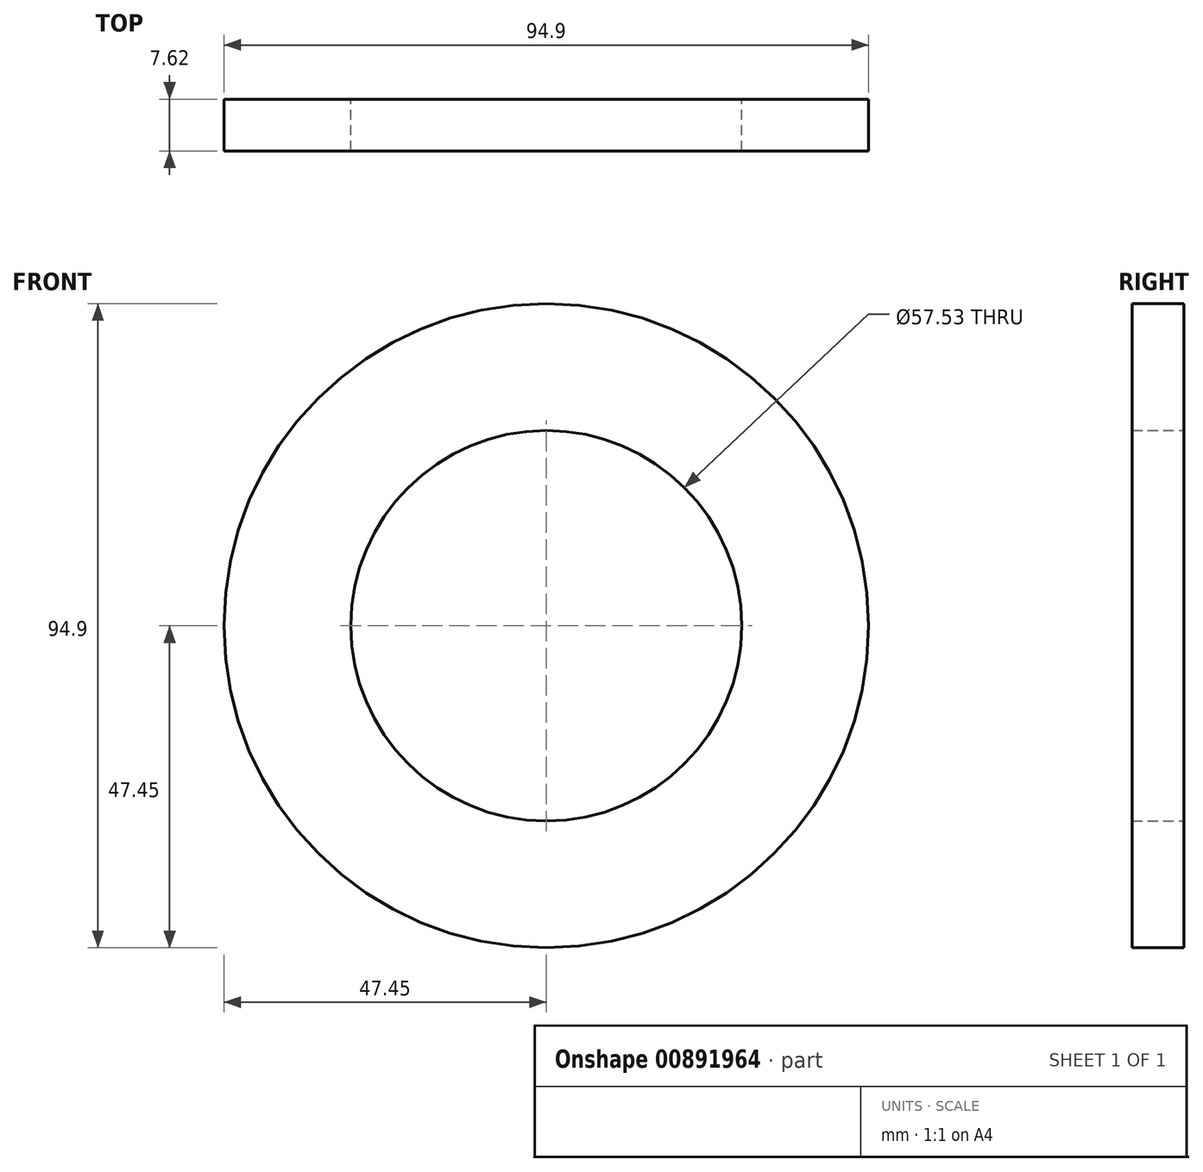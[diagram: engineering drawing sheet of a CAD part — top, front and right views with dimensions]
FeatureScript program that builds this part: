
annotation { "Feature Type Name" : "Feature", "Feature Type Description" : "" }
export const myFeature = defineFeature(function(context is Context, id is Id, definition is map)
    precondition{}
    {
        {
            var Q0;
            Q0=qCreatedBy(makeId("Front.planeOp"),FACE);
            var sketch = newSketch(context, id + "F0", { "sketchPlane" : qUnion([Q0])});
            skCircle(sketch, "E0", {"center": v(0, 0) * mm, "radius": 47.45 * mm});
            skCircle(sketch, "E1", {"center": v(0, 0) * mm, "radius": 28.76 * mm});
            skSolve(sketch);
        }
        {
            var Q0;
            Q0 = qSketchRegion(id + "F0", true);
            extrude(context, id + "F1", {"entities" : qUnion([Q0]), "depth" : 7.62 * mm, "offsetDistance" : 25.4 * mm});
        }
    });
